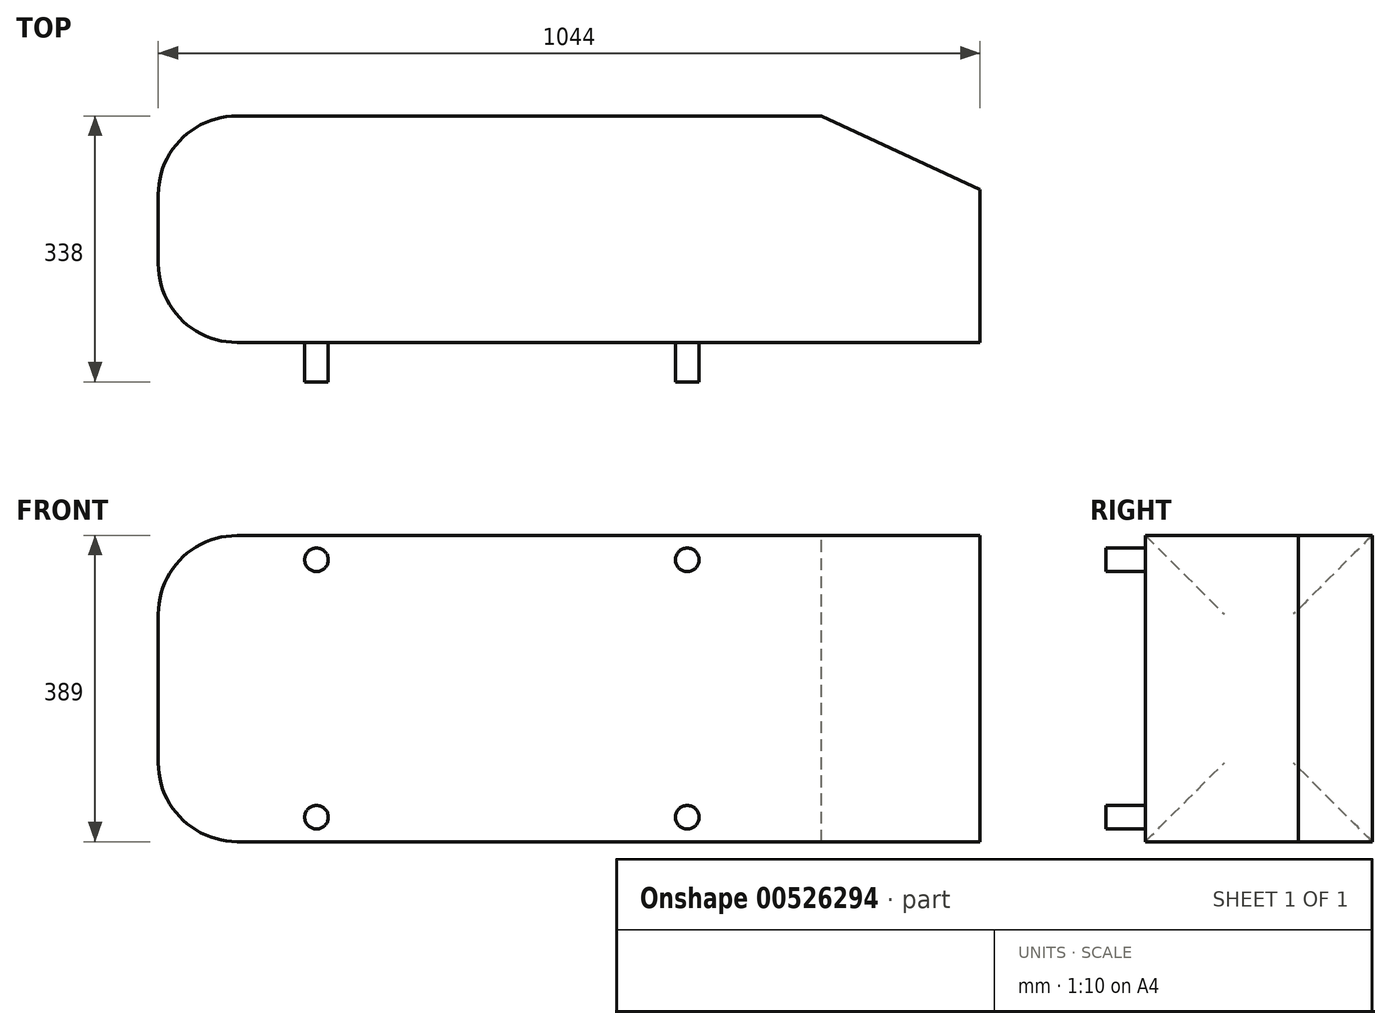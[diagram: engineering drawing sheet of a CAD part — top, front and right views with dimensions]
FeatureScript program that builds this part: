
annotation { "Feature Type Name" : "Feature", "Feature Type Description" : "" }
export const myFeature = defineFeature(function(context is Context, id is Id, definition is map)
    precondition{}
    {
        {
            var Q0;
            Q0=qCreatedBy(makeId("Front.planeOp"),FACE);
            var sketch = newSketch(context, id + "F0", { "sketchPlane" : qUnion([Q0])});
            skLineSegment(sketch, "E0.bottom", {"start": v(-509.9, -194.5) * mm, "end": v(534.1, -194.5) * mm});
            skLineSegment(sketch, "E0.top", {"start": v(-509.9, 194.5) * mm, "end": v(534.1, 194.5) * mm});
            skLineSegment(sketch, "E0.left", {"start": v(-509.9, -194.5) * mm, "end": v(-509.9, 194.5) * mm});
            skLineSegment(sketch, "E0.right", {"start": v(534.1, -194.5) * mm, "end": v(534.1, 194.5) * mm});
            skSolve(sketch);
        }
        {
            var Q0;
            Q0=makeQuery(id+"F0.imprint","IMPRINT",FACE,{"disambiguationData":[TD([[makeQuery(id+"F0.imprint","IMPRINT",EDGE,{"derivedFrom":sQuery(id+"F0.wireOp",EDGE,"E0.bottom")}),1.0]])]});
            extrude(context, id + "F1", {"entities" : qUnion([Q0]), "oppositeDirection" : true, "depth" : 288 * mm, "offsetDistance" : 25 * mm});
        }
        {
            var Q0;
            Q0=makeQuery(id+"F1.opExtrude","SWEPT_EDGE",EDGE,{"disambiguationData":[OSD([sQuery(id+"F0.wireOp",EDGE,"E0.top"),sQuery(id+"F0.wireOp",EDGE,"E0.left")])]});
            var Q1;
            Q1=makeQuery(id+"F1.opExtrude","CAP_EDGE",EDGE,{"disambiguationData":[OSD([sQuery(id+"F0.wireOp",EDGE,"E0.left")])],"isStart":false});
            var Q2;
            Q2=makeQuery(id+"F1.opExtrude","SWEPT_EDGE",EDGE,{"disambiguationData":[OSD([sQuery(id+"F0.wireOp",EDGE,"E0.bottom"),sQuery(id+"F0.wireOp",EDGE,"E0.left")])]});
            var Q3;
            Q3=makeQuery(id+"F1.opExtrude","CAP_EDGE",EDGE,{"disambiguationData":[OSD([sQuery(id+"F0.wireOp",EDGE,"E0.left")])],"isStart":true});
            fillet(context, id + "F2", {"entities" : qUnion([Q0, Q1, Q2, Q3]), "radius" : 100 * mm, "tangentPropagation" : true, "allowEdgeOverflow" : false});
        }
        {
            var Q0;
            Q0=makeQuery(id+"F1.opExtrude","SWEPT_FACE",FACE,{"disambiguationData":[OSD([sQuery(id+"F0.wireOp",EDGE,"E0.top")])]});
            var sketch = newSketch(context, id + "F3", { "sketchPlane" : qUnion([Q0])});
            skLineSegment(sketch, "E1", {"start": v(332.9, 288) * mm, "end": v(534.1, 194.18) * mm});
            skLineSegment(sketch, "E2", {"start": v(534.1, 194.18) * mm, "end": v(534.1, 288) * mm});
            skLineSegment(sketch, "E3", {"start": v(534.1, 288) * mm, "end": v(332.9, 288) * mm});
            skSolve(sketch);
        }
        {
            var Q0;
            Q0=makeQuery(id+"F3.imprint","IMPRINT",FACE,{"disambiguationData":[TD([[makeQuery(id+"F3.imprint","IMPRINT",EDGE,{"derivedFrom":sQuery(id+"F3.wireOp",EDGE,"E1")}),1.0]])]});
            extrude(context, id + "F4", {"entities" : qUnion([Q0]), "operationType" : NewBodyOperationType.REMOVE, "endBound" : BoundingType.THROUGH_ALL, "oppositeDirection" : true, "depth" : 25 * mm, "offsetDistance" : 25 * mm});
        }
        {
            var Q0;
            Q0=makeQuery(id+"F1.opExtrude","CAP_FACE",FACE,{"disambiguationData":[OSD([sQuery(id+"F0.wireOp",EDGE,"E0.bottom"),sQuery(id+"F0.wireOp",EDGE,"E0.top"),sQuery(id+"F0.wireOp",EDGE,"E0.left"),sQuery(id+"F0.wireOp",EDGE,"E0.right")])],"isStart":true});
            var sketch = newSketch(context, id + "F5", { "sketchPlane" : qUnion([Q0])});
            skCircle(sketch, "E4", {"center": v(162.1, -163.5) * mm, "radius": 15 * mm});
            skCircle(sketch, "E5", {"center": v(-308.9, -163.5) * mm, "radius": 15 * mm});
            skLineSegment(sketch, "E6", {"start": v(-554.1, 0) * mm, "end": v(655.24, 0) * mm, "construction": true});
            skCircle(sketch, "E7.MirrorC", {"center": v(162.1, 163.5) * mm, "radius": 15 * mm});
            skCircle(sketch, "E8.MirrorC", {"center": v(-308.9, 163.5) * mm, "radius": 15 * mm});
            skSolve(sketch);
        }
        {
            var Q0;
            Q0 = qSketchRegion(id + "F5", true);
            extrude(context, id + "F6", {"entities" : qUnion([Q0]), "operationType" : NewBodyOperationType.ADD, "depth" : 50 * mm, "offsetDistance" : 25 * mm});
        }
        {
            var Q0;
            Q0=makeQuery(id+"F1.opExtrude","SWEPT_BODY",BODY,{"disambiguationData":[OSD([sQuery(id+"F0.wireOp",EDGE,"E0.bottom"),sQuery(id+"F0.wireOp",EDGE,"E0.top"),sQuery(id+"F0.wireOp",EDGE,"E0.left"),sQuery(id+"F0.wireOp",EDGE,"E0.right")])]});
            transform(context, id + "F7", {"entities" : qUnion([Q0]), "transformType" : TransformType.TRANSLATION_3D, "dx" : 0 * mm, "dy" : 50 * mm, "dz" : 0 * mm, "makeCopy" : false});
        }
    });
